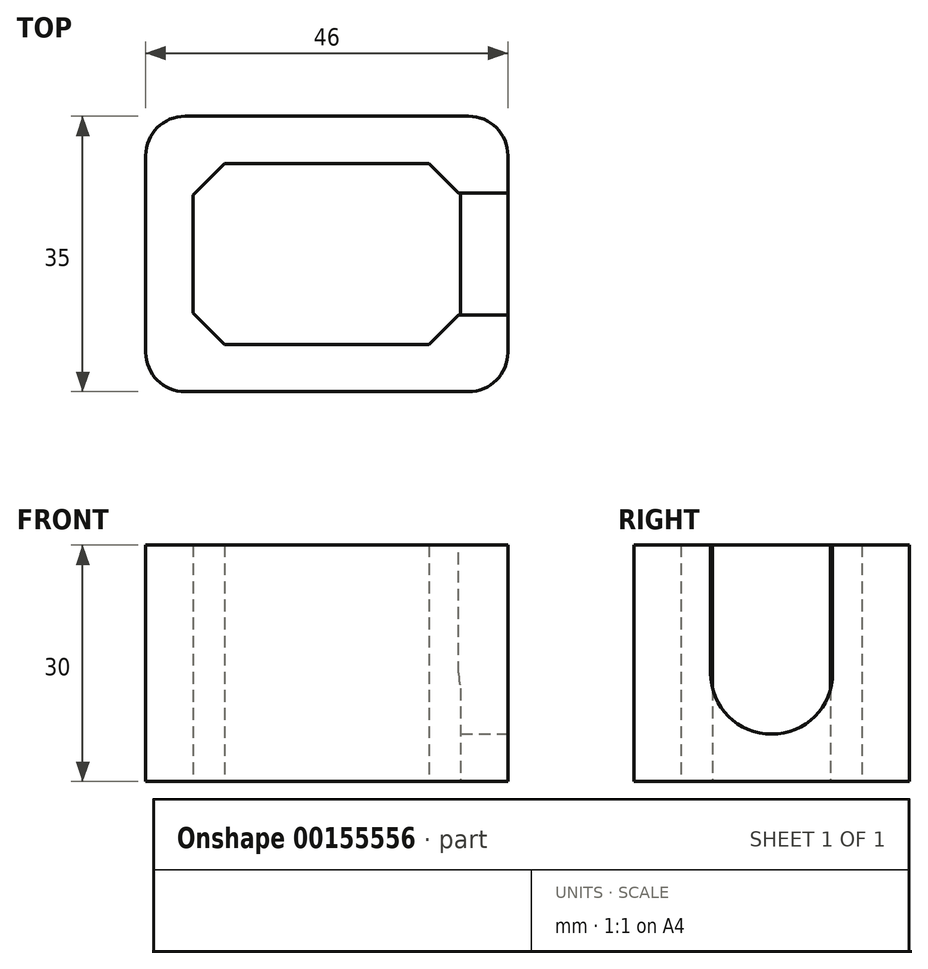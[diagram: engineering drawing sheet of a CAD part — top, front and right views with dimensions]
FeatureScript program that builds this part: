
annotation { "Feature Type Name" : "Feature", "Feature Type Description" : "" }
export const myFeature = defineFeature(function(context is Context, id is Id, definition is map)
    precondition{}
    {
        {
            var Q0;
            Q0=qCreatedBy(makeId("Top.planeOp"),FACE);
            var sketch = newSketch(context, id + "F0", { "sketchPlane" : qUnion([Q0])});
            skLineSegment(sketch, "E0", {"start": v(-13, 11.5) * mm, "end": v(13, 11.5) * mm});
            skLineSegment(sketch, "E1", {"start": v(13, 11.5) * mm, "end": v(17, 7.5) * mm});
            skLineSegment(sketch, "E2", {"start": v(17, 7.5) * mm, "end": v(17, -7.5) * mm});
            skLineSegment(sketch, "E3", {"start": v(17, -7.5) * mm, "end": v(13, -11.5) * mm});
            skLineSegment(sketch, "E4", {"start": v(13, -11.5) * mm, "end": v(-13, -11.5) * mm});
            skLineSegment(sketch, "E5", {"start": v(-13, -11.5) * mm, "end": v(-17, -7.5) * mm});
            skLineSegment(sketch, "E6", {"start": v(-17, -7.5) * mm, "end": v(-17, 7.5) * mm});
            skLineSegment(sketch, "E7", {"start": v(-17, 7.5) * mm, "end": v(-13, 11.5) * mm});
            skLineSegment(sketch, "E8.bottom", {"start": v(23, -17.5) * mm, "end": v(-23, -17.5) * mm});
            skLineSegment(sketch, "E8.top", {"start": v(23, 17.5) * mm, "end": v(-23, 17.5) * mm});
            skLineSegment(sketch, "E8.left", {"start": v(23, -17.5) * mm, "end": v(23, 17.5) * mm});
            skLineSegment(sketch, "E8.right", {"start": v(-23, -17.5) * mm, "end": v(-23, 17.5) * mm});
            skPoint(sketch, "E8.middle", {"position": v(0, 0) * mm});
            skSolve(sketch);
        }
        {
            var Q0;
            Q0 = qSketchRegion(id + "F0", true);
            extrude(context, id + "F1", {"entities" : qUnion([Q0]), "depth" : 30 * mm});
        }
        {
            var Q0;
            Q0=makeQuery(id+"F1.opExtrude","SWEPT_FACE",FACE,{"disambiguationData":[OSD([sQuery(id+"F0.wireOp",EDGE,"E8.left")])]});
            var sketch = newSketch(context, id + "F2", { "sketchPlane" : qUnion([Q0])});
            skArc(sketch, "E9", {"start": v(-7.75, 13.75) * mm, "mid": v(0, 6) * mm, "end": v(7.75, 13.75) * mm});
            skLineSegment(sketch, "E10", {"start": v(7.75, 30) * mm, "end": v(7.75, 13.75) * mm});
            skLineSegment(sketch, "E11", {"start": v(-7.75, 30) * mm, "end": v(-7.75, 13.75) * mm});
            skLineSegment(sketch, "E12", {"start": v(-7.75, 30) * mm, "end": v(7.75, 30) * mm});
            skSolve(sketch);
        }
        {
            var Q0;
            Q0 = qSketchRegion(id + "F2", true);
            extrude(context, id + "F3", {"entities" : qUnion([Q0]), "operationType" : NewBodyOperationType.REMOVE, "endBound" : BoundingType.UP_TO_NEXT, "oppositeDirection" : true, "depth" : 25 * mm});
        }
        {
            var Q0;
            Q0=makeQuery(id+"F1.opExtrude","SWEPT_EDGE",EDGE,{"disambiguationData":[OSD([sQuery(id+"F0.wireOp",EDGE,"E8.bottom"),sQuery(id+"F0.wireOp",EDGE,"E8.left")])]});
            var Q1;
            Q1=makeQuery(id+"F1.opExtrude","SWEPT_EDGE",EDGE,{"disambiguationData":[OSD([sQuery(id+"F0.wireOp",EDGE,"E8.top"),sQuery(id+"F0.wireOp",EDGE,"E8.left")])]});
            var Q2;
            Q2=makeQuery(id+"F1.opExtrude","SWEPT_EDGE",EDGE,{"disambiguationData":[OSD([sQuery(id+"F0.wireOp",EDGE,"E8.top"),sQuery(id+"F0.wireOp",EDGE,"E8.right")])]});
            var Q3;
            Q3=makeQuery(id+"F1.opExtrude","SWEPT_EDGE",EDGE,{"disambiguationData":[OSD([sQuery(id+"F0.wireOp",EDGE,"E8.bottom"),sQuery(id+"F0.wireOp",EDGE,"E8.right")])]});
            fillet(context, id + "F4", {"entities" : qUnion([Q0, Q1, Q2, Q3]), "radius" : 5 * mm, "tangentPropagation" : true, "allowEdgeOverflow" : false});
        }
    });
